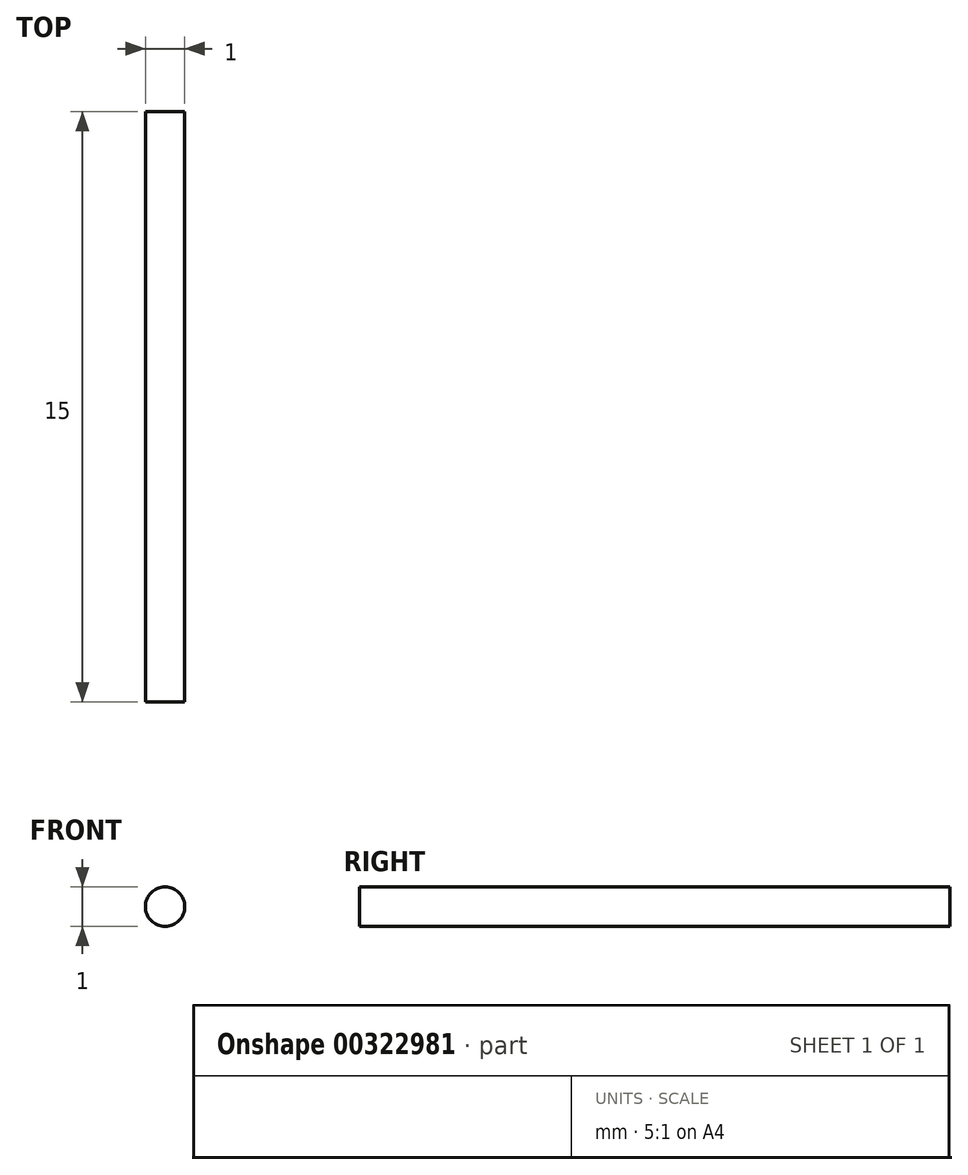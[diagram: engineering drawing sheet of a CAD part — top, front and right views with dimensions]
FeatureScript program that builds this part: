
annotation { "Feature Type Name" : "Feature", "Feature Type Description" : "" }
export const myFeature = defineFeature(function(context is Context, id is Id, definition is map)
    precondition{}
    {
        {
            var Q0;
            Q0=qCreatedBy(makeId("Front.planeOp"),FACE);
            var sketch = newSketch(context, id + "F0", { "sketchPlane" : qUnion([Q0])});
            skCircle(sketch, "E0", {"center": v(0, 0) * mm, "radius": 0.5 * mm});
            skSolve(sketch);
        }
        {
            var Q0;
            Q0 = qSketchRegion(id + "F0", true);
            extrude(context, id + "F1", {"entities" : qUnion([Q0]), "depth" : 15 * mm});
        }
    });
